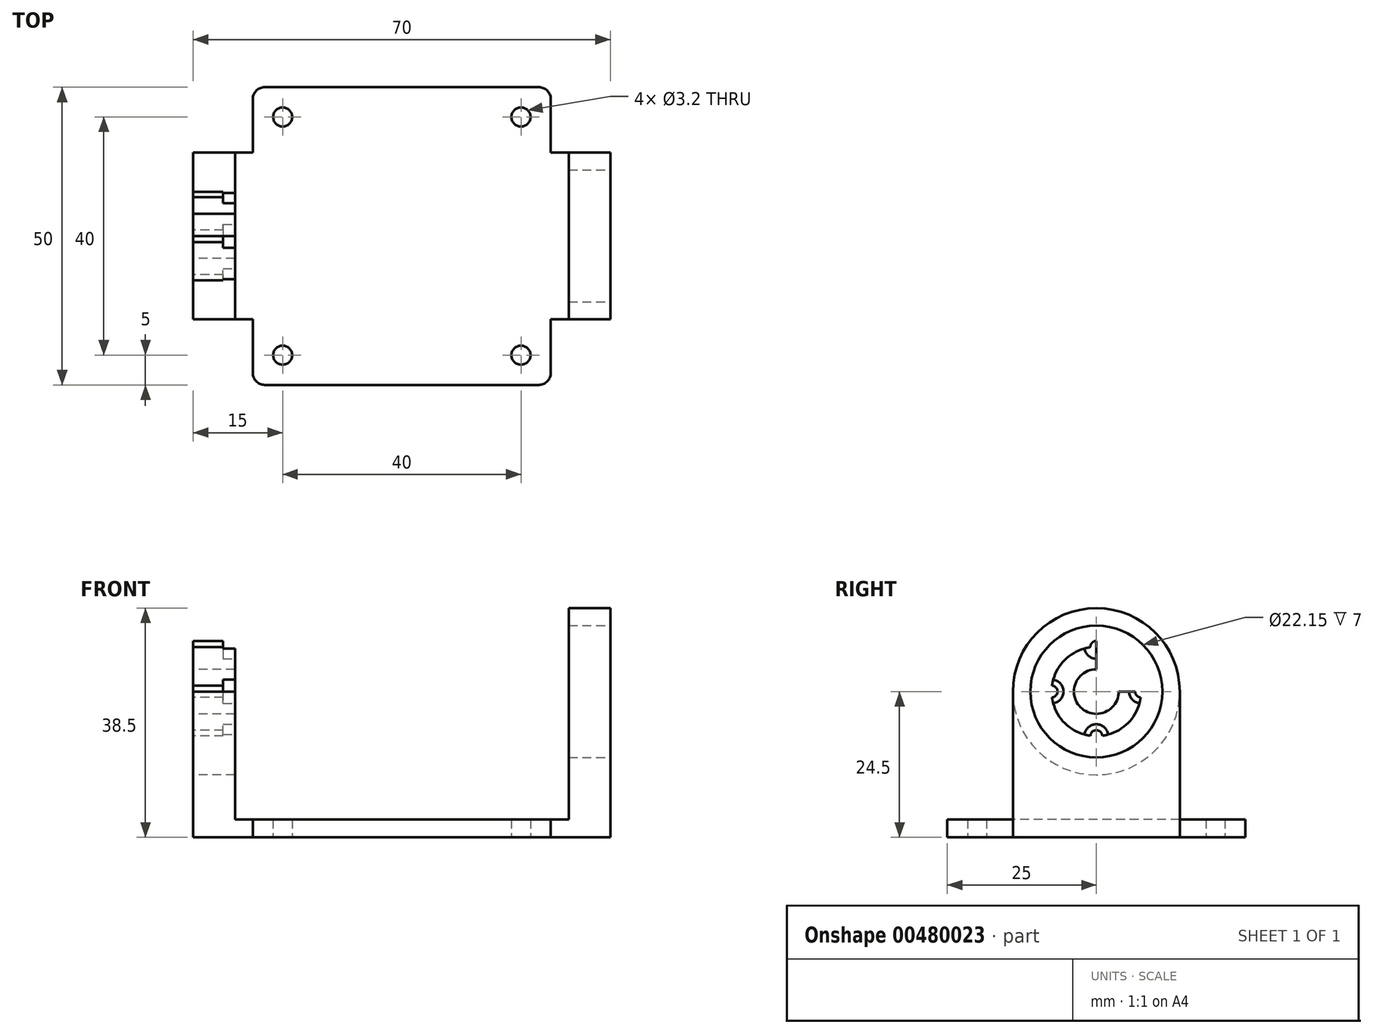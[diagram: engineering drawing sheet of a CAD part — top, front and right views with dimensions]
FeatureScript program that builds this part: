
annotation { "Feature Type Name" : "Feature", "Feature Type Description" : "" }
export const myFeature = defineFeature(function(context is Context, id is Id, definition is map)
    precondition{}
    {
        {
            var Q0;
            Q0=qCreatedBy(makeId("Top.planeOp"),FACE);
            var sketch = newSketch(context, id + "F0", { "sketchPlane" : qUnion([Q0])});
            skLineSegment(sketch, "E0.bottom", {"start": v(23, 25) * mm, "end": v(-23, 25) * mm});
            skLineSegment(sketch, "E0.top", {"start": v(23, -25) * mm, "end": v(-23, -25) * mm});
            skLineSegment(sketch, "E0.left", {"start": v(25, 23) * mm, "end": v(25, -23) * mm});
            skLineSegment(sketch, "E0.right", {"start": v(-25, 23) * mm, "end": v(-25, -23) * mm});
            skPoint(sketch, "E0.middle", {"position": v(0, 0) * mm});
            skLineSegment(sketch, "E1.bottom", {"start": v(-20, 20) * mm, "end": v(20, 20) * mm});
            skLineSegment(sketch, "E1.top", {"start": v(-20, -20) * mm, "end": v(20, -20) * mm});
            skLineSegment(sketch, "E1.left", {"start": v(-20, 20) * mm, "end": v(-20, -20) * mm});
            skLineSegment(sketch, "E1.right", {"start": v(20, 20) * mm, "end": v(20, -20) * mm});
            skCircle(sketch, "E2", {"center": v(-20, 20) * mm, "radius": 1.6 * mm});
            skCircle(sketch, "E3", {"center": v(20, 20) * mm, "radius": 1.6 * mm});
            skCircle(sketch, "E4", {"center": v(-20, -20) * mm, "radius": 1.6 * mm});
            skCircle(sketch, "E5", {"center": v(20, -20) * mm, "radius": 1.6 * mm});
            skLineSegment(sketch, "E6.bottom", {"start": v(-25, 0) * mm, "end": v(-35, 0) * mm});
            skLineSegment(sketch, "E6.top", {"start": v(-25, 14) * mm, "end": v(-35, 14) * mm});
            skLineSegment(sketch, "E6.left", {"start": v(-25, 0) * mm, "end": v(-25, 14) * mm});
            skLineSegment(sketch, "E6.right", {"start": v(-35, 0) * mm, "end": v(-35, 14) * mm});
            skLineSegment(sketch, "E7.top", {"start": v(-25, -14) * mm, "end": v(-35, -14) * mm});
            skLineSegment(sketch, "E7.left", {"start": v(-25, 0) * mm, "end": v(-25, -14) * mm});
            skLineSegment(sketch, "E7.right", {"start": v(-35, 0) * mm, "end": v(-35, -14) * mm});
            skLineSegment(sketch, "E8.bottom", {"start": v(25, 0) * mm, "end": v(35, 0) * mm});
            skLineSegment(sketch, "E8.top", {"start": v(25, 14) * mm, "end": v(35, 14) * mm});
            skLineSegment(sketch, "E8.left", {"start": v(25, 0) * mm, "end": v(25, 14) * mm});
            skLineSegment(sketch, "E8.right", {"start": v(35, 0) * mm, "end": v(35, 14) * mm});
            skLineSegment(sketch, "E9.top", {"start": v(25, -14) * mm, "end": v(35, -14) * mm});
            skLineSegment(sketch, "E9.left", {"start": v(25, 0) * mm, "end": v(25, -14) * mm});
            skLineSegment(sketch, "E9.right", {"start": v(35, 0) * mm, "end": v(35, -14) * mm});
            skPoint(sketch, "E10.visualSharp", {"position": v(-25, 25) * mm});
            skArc(sketch, "E10.filletArc", {"start": v(-23, 25) * mm, "mid": v(-24.41, 24.41) * mm, "end": v(-25, 23) * mm});
            skPoint(sketch, "E11.visualSharp", {"position": v(-25, -25) * mm});
            skArc(sketch, "E11.filletArc", {"start": v(-25, -23) * mm, "mid": v(-24.41, -24.41) * mm, "end": v(-23, -25) * mm});
            skPoint(sketch, "E12.visualSharp", {"position": v(25, 25) * mm});
            skArc(sketch, "E12.filletArc", {"start": v(25, 23) * mm, "mid": v(24.41, 24.41) * mm, "end": v(23, 25) * mm});
            skPoint(sketch, "E13.visualSharp", {"position": v(25, -25) * mm});
            skArc(sketch, "E13.filletArc", {"start": v(23, -25) * mm, "mid": v(24.41, -24.41) * mm, "end": v(25, -23) * mm});
            skSolve(sketch);
        }
        {
            var Q0;
            Q0 = qSketchRegion(id + "F0", true);
            var Q1;
            {var subQ5=sQuery(id+"F0.wireOp",EDGE,"E2");var subQ13=sQuery(id+"F0.wireOp",EDGE,"E1.bottom");var subQ14=makeQuery(id+"F0.imprint","INTERSECT",VERTEX,{"derivedFrom":[subQ13,subQ5]});Q1=makeQuery(id+"F0.imprint","IMPRINT",FACE,{"disambiguationData":[TD([[makeQuery(id+"F0.imprint","IMPRINT",EDGE,{"disambiguationData":[TD([[subQ14,-1.0]])],"derivedFrom":subQ13}),-1.0]])]});}
            extrude(context, id + "F1", {"entities" : qUnion([Q0, Q1]), "depth" : 3 * mm});
        }
        {
            var Q0;
            Q0=makeQuery(id+"F1.opExtrude","CAP_FACE",FACE,{"disambiguationData":[OSD([sQuery(id+"F0.wireOp",EDGE,"E0.bottom"),sQuery(id+"F0.wireOp",EDGE,"E0.top"),sQuery(id+"F0.wireOp",EDGE,"E0.left"),sQuery(id+"F0.wireOp",EDGE,"E0.right"),sQuery(id+"F0.wireOp",EDGE,"E2"),sQuery(id+"F0.wireOp",EDGE,"E3"),sQuery(id+"F0.wireOp",EDGE,"E4"),sQuery(id+"F0.wireOp",EDGE,"E5"),sQuery(id+"F0.wireOp",EDGE,"E6.top"),sQuery(id+"F0.wireOp",EDGE,"E6.right"),sQuery(id+"F0.wireOp",EDGE,"E7.top"),sQuery(id+"F0.wireOp",EDGE,"E7.right"),sQuery(id+"F0.wireOp",EDGE,"E8.top"),sQuery(id+"F0.wireOp",EDGE,"E8.right"),sQuery(id+"F0.wireOp",EDGE,"E9.top"),sQuery(id+"F0.wireOp",EDGE,"E9.right"),sQuery(id+"F0.wireOp",EDGE,"E10.filletArc"),sQuery(id+"F0.wireOp",EDGE,"E11.filletArc"),sQuery(id+"F0.wireOp",EDGE,"E12.filletArc"),sQuery(id+"F0.wireOp",EDGE,"E13.filletArc")])],"isStart":false});
            var sketch = newSketch(context, id + "F2", { "sketchPlane" : qUnion([Q0])});
            skLineSegment(sketch, "E14.bottom", {"start": v(-35, 14) * mm, "end": v(-28, 14) * mm});
            skLineSegment(sketch, "E14.top", {"start": v(-35, -14) * mm, "end": v(-28, -14) * mm});
            skLineSegment(sketch, "E14.left", {"start": v(-35, 14) * mm, "end": v(-35, -14) * mm});
            skLineSegment(sketch, "E14.right", {"start": v(-28, 14) * mm, "end": v(-28, -14) * mm});
            skLineSegment(sketch, "E15.bottom", {"start": v(35, 14) * mm, "end": v(28, 14) * mm});
            skLineSegment(sketch, "E15.top", {"start": v(35, -14) * mm, "end": v(28, -14) * mm});
            skLineSegment(sketch, "E15.left", {"start": v(35, 14) * mm, "end": v(35, -14) * mm});
            skLineSegment(sketch, "E15.right", {"start": v(28, 14) * mm, "end": v(28, -14) * mm});
            skSolve(sketch);
        }
        {
            var Q0;
            Q0 = qSketchRegion(id + "F2", true);
            extrude(context, id + "F3", {"entities" : qUnion([Q0]), "operationType" : NewBodyOperationType.ADD, "depth" : (32 + 3.5) * mm});
        }
        {
            var Q0;
            Q0=makeQuery(id+"F3.boolean.opBoolean","MERGE",FACE,{"derivedFrom":[makeQuery(id+"F1.opExtrude","SWEPT_FACE",FACE,{"disambiguationData":[OSD([sQuery(id+"F0.wireOp",EDGE,"E6.right"),sQuery(id+"F0.wireOp",EDGE,"E7.right")])]}),makeQuery(id+"F3.opExtrude","SWEPT_FACE",FACE,{"disambiguationData":[OSD([sQuery(id+"F2.wireOp",EDGE,"E14.left")])]})]});
            var sketch = newSketch(context, id + "F4", { "sketchPlane" : qUnion([Q0])});
            skLineSegment(sketch, "E16", {"start": v(0, 38.5) * mm, "end": v(0, 24.5) * mm});
            skPoint(sketch, "E16.endSnap0", {"position": v(0, 38.5) * mm});
            skCircle(sketch, "E17", {"center": v(0, 24.5) * mm, "radius": 11 * mm});
            skCircle(sketch, "E18", {"center": v(0, 24.5) * mm, "radius": 14 * mm});
            skLineSegment(sketch, "E19.bottom", {"start": v(-14, 38.5) * mm, "end": v(14, 38.5) * mm});
            skLineSegment(sketch, "E19.top", {"start": v(-14, 0) * mm, "end": v(14, 0) * mm});
            skLineSegment(sketch, "E19.left", {"start": v(-14, 38.5) * mm, "end": v(-14, 0) * mm});
            skLineSegment(sketch, "E19.right", {"start": v(14, 38.5) * mm, "end": v(14, 0) * mm});
            skSolve(sketch);
        }
        {
            var Q0;
            {var subQ0=sQuery(id+"F4.wireOp",EDGE,"E19.bottom");var subQ1=sQuery(id+"F4.wireOp",EDGE,"E18");var subQ2=makeQuery(id+"F4.imprint","INTERSECT",VERTEX,{"derivedFrom":[subQ1,subQ0]});Q0=makeQuery(id+"F4.imprint","IMPRINT",FACE,{"disambiguationData":[TD([[makeQuery(id+"F4.imprint","IMPRINT",EDGE,{"disambiguationData":[TD([[subQ2,1.0]])],"derivedFrom":subQ1}),-1.0]])]});}
            var Q1;
            {var subQ0=sQuery(id+"F4.wireOp",EDGE,"E19.bottom");var subQ1=sQuery(id+"F4.wireOp",EDGE,"E18");var subQ2=makeQuery(id+"F4.imprint","INTERSECT",VERTEX,{"derivedFrom":[subQ1,subQ0]});Q1=makeQuery(id+"F4.imprint","IMPRINT",FACE,{"disambiguationData":[TD([[makeQuery(id+"F4.imprint","IMPRINT",EDGE,{"disambiguationData":[TD([[subQ2,-1.0]])],"derivedFrom":subQ1}),-1.0]])]});}
            extrude(context, id + "F5", {"entities" : qUnion([Q0, Q1]), "operationType" : NewBodyOperationType.REMOVE, "endBound" : BoundingType.THROUGH_ALL, "oppositeDirection" : true, "depth" : 25 * mm});
        }
        {
            var Q0;
            Q0=makeQuery(id+"F3.boolean.opBoolean","MERGE",FACE,{"derivedFrom":[makeQuery(id+"F1.opExtrude","SWEPT_FACE",FACE,{"disambiguationData":[OSD([sQuery(id+"F0.wireOp",EDGE,"E8.right"),sQuery(id+"F0.wireOp",EDGE,"E9.right")])]}),makeQuery(id+"F3.opExtrude","SWEPT_FACE",FACE,{"disambiguationData":[OSD([sQuery(id+"F2.wireOp",EDGE,"E15.left")])]})]});
            var sketch = newSketch(context, id + "F6", { "sketchPlane" : qUnion([Q0])});
            skCircle(sketch, "E20", {"center": v(0, 24.5) * mm, "radius": 14 * mm});
            skPoint(sketch, "E20.first.point", {"position": v(-14, 24.5) * mm});
            skPoint(sketch, "E20.second.point", {"position": v(0, 38.5) * mm});
            skPoint(sketch, "E20.third.point", {"position": v(14, 24.5) * mm});
            skCircle(sketch, "E21", {"center": v(0, 24.5) * mm, "radius": 11.07 * mm});
            skSolve(sketch);
        }
        {
            var Q0;
            Q0=makeQuery(id+"F6.imprint","IMPRINT",FACE,{"disambiguationData":[TD([[makeQuery(id+"F6.imprint","IMPRINT",EDGE,{"derivedFrom":sQuery(id+"F6.wireOp",EDGE,"E21")}),1.0]])]});
            extrude(context, id + "F7", {"entities" : qUnion([Q0]), "operationType" : NewBodyOperationType.REMOVE, "endBound" : BoundingType.UP_TO_NEXT, "oppositeDirection" : true, "depth" : 25 * mm});
        }
        {
            var Q0;
            Q0=makeQuery(id+"F3.boolean.opBoolean","MERGE",FACE,{"derivedFrom":[makeQuery(id+"F1.opExtrude","SWEPT_FACE",FACE,{"disambiguationData":[OSD([sQuery(id+"F0.wireOp",EDGE,"E6.right"),sQuery(id+"F0.wireOp",EDGE,"E7.right")])]}),makeQuery(id+"F3.opExtrude","SWEPT_FACE",FACE,{"disambiguationData":[OSD([sQuery(id+"F2.wireOp",EDGE,"E14.left")])]})]});
            var sketch = newSketch(context, id + "F8", { "sketchPlane" : qUnion([Q0])});
            skCircle(sketch, "E22", {"center": v(0, 24.5) * mm, "radius": 14 * mm});
            skPoint(sketch, "E22.first.point", {"position": v(-14, 24.5) * mm});
            skPoint(sketch, "E22.second.point", {"position": v(0, 38.5) * mm});
            skPoint(sketch, "E22.third.point", {"position": v(14, 24.5) * mm});
            skCircle(sketch, "E23", {"center": v(0, 24.5) * mm, "radius": 7.5 * mm});
            skLineSegment(sketch, "E24", {"start": v(0, 38.5) * mm, "end": v(0, 17) * mm});
            skLineSegment(sketch, "E25", {"start": v(0, 24.5) * mm, "end": v(7.5, 24.5) * mm});
            skLineSegment(sketch, "E26", {"start": v(0, 24.5) * mm, "end": v(-7.5, 24.5) * mm});
            skCircle(sketch, "E27", {"center": v(0, 32) * mm, "radius": 1 * mm});
            skCircle(sketch, "E28", {"center": v(-7.5, 24.5) * mm, "radius": 1 * mm});
            skCircle(sketch, "E29", {"center": v(7.5, 24.5) * mm, "radius": 1 * mm});
            skCircle(sketch, "E30", {"center": v(0, 17) * mm, "radius": 1 * mm});
            skCircle(sketch, "E31", {"center": v(0, 24.5) * mm, "radius": 3.75 * mm});
            skSolve(sketch);
        }
        {
            var Q0;
            {var subQ1=sQuery(id+"F8.wireOp",EDGE,"E24");var subQ3=sQuery(id+"F8.wireOp",EDGE,"E31");var subQ4=makeQuery(id+"F8.imprint","INTERSECT",VERTEX,{"disambiguationData":[OD(1.0)],"derivedFrom":[subQ1,subQ3]});Q0=makeQuery(id+"F8.imprint","IMPRINT",FACE,{"disambiguationData":[TD([[makeQuery(id+"F8.imprint","IMPRINT",EDGE,{"disambiguationData":[TD([[subQ4,1.0]])],"derivedFrom":subQ3}),1.0]])]});}
            var Q1;
            {var subQ1=sQuery(id+"F8.wireOp",EDGE,"E24");var subQ3=sQuery(id+"F8.wireOp",EDGE,"E31");var subQ4=makeQuery(id+"F8.imprint","INTERSECT",VERTEX,{"disambiguationData":[OD(0.0)],"derivedFrom":[subQ1,subQ3]});Q1=makeQuery(id+"F8.imprint","IMPRINT",FACE,{"disambiguationData":[TD([[makeQuery(id+"F8.imprint","IMPRINT",EDGE,{"disambiguationData":[TD([[subQ4,-1.0]])],"derivedFrom":subQ3}),1.0]])]});}
            var Q2;
            {var subQ1=sQuery(id+"F8.wireOp",EDGE,"E24");var subQ3=sQuery(id+"F8.wireOp",EDGE,"E31");var subQ4=makeQuery(id+"F8.imprint","INTERSECT",VERTEX,{"disambiguationData":[OD(0.0)],"derivedFrom":[subQ1,subQ3]});Q2=makeQuery(id+"F8.imprint","IMPRINT",FACE,{"disambiguationData":[TD([[makeQuery(id+"F8.imprint","IMPRINT",EDGE,{"disambiguationData":[TD([[subQ4,1.0]])],"derivedFrom":subQ3}),1.0]])]});}
            var Q3;
            {var subQ1=sQuery(id+"F8.wireOp",EDGE,"E24");var subQ3=sQuery(id+"F8.wireOp",EDGE,"E31");var subQ4=makeQuery(id+"F8.imprint","INTERSECT",VERTEX,{"disambiguationData":[OD(1.0)],"derivedFrom":[subQ1,subQ3]});Q3=makeQuery(id+"F8.imprint","IMPRINT",FACE,{"disambiguationData":[TD([[makeQuery(id+"F8.imprint","IMPRINT",EDGE,{"disambiguationData":[TD([[subQ4,-1.0]])],"derivedFrom":subQ3}),1.0]])]});}
            var Q4;
            {var subQ0=sQuery(id+"F8.wireOp",EDGE,"E23");var subQ1=makeQuery(id+"F8.imprint","INTERSECT",VERTEX,{"derivedFrom":[subQ0,sQuery(id+"F8.wireOp",EDGE,"E26")]});Q4=makeQuery(id+"F8.imprint","IMPRINT",FACE,{"disambiguationData":[TD([[makeQuery(id+"F8.imprint","IMPRINT",EDGE,{"disambiguationData":[TD([[subQ1,1.0]])],"derivedFrom":subQ0}),-1.0]])]});}
            var Q5;
            {var subQ0=sQuery(id+"F8.wireOp",EDGE,"E26");var subQ1=sQuery(id+"F8.wireOp",EDGE,"E23");var subQ2=makeQuery(id+"F8.imprint","INTERSECT",VERTEX,{"derivedFrom":[subQ1,subQ0]});Q5=makeQuery(id+"F8.imprint","IMPRINT",FACE,{"disambiguationData":[TD([[makeQuery(id+"F8.imprint","IMPRINT",EDGE,{"disambiguationData":[TD([[subQ2,1.0]])],"derivedFrom":subQ1}),1.0]])]});}
            var Q6;
            {var subQ0=sQuery(id+"F8.wireOp",EDGE,"E26");var subQ1=sQuery(id+"F8.wireOp",EDGE,"E23");var subQ2=makeQuery(id+"F8.imprint","INTERSECT",VERTEX,{"derivedFrom":[subQ1,subQ0]});Q6=makeQuery(id+"F8.imprint","IMPRINT",FACE,{"disambiguationData":[TD([[makeQuery(id+"F8.imprint","IMPRINT",EDGE,{"disambiguationData":[TD([[subQ2,-1.0]])],"derivedFrom":subQ1}),1.0]])]});}
            var Q7;
            {var subQ0=sQuery(id+"F8.wireOp",EDGE,"E24");var subQ1=sQuery(id+"F8.wireOp",EDGE,"E23");var subQ2=makeQuery(id+"F8.imprint","INTERSECT",VERTEX,{"disambiguationData":[OD(1.0)],"derivedFrom":[subQ1,subQ0]});Q7=makeQuery(id+"F8.imprint","IMPRINT",FACE,{"disambiguationData":[TD([[makeQuery(id+"F8.imprint","IMPRINT",EDGE,{"disambiguationData":[TD([[subQ2,-1.0]])],"derivedFrom":subQ1}),-1.0]])]});}
            var Q8;
            {var subQ0=sQuery(id+"F8.wireOp",EDGE,"E24");var subQ1=sQuery(id+"F8.wireOp",EDGE,"E23");var subQ2=makeQuery(id+"F8.imprint","INTERSECT",VERTEX,{"disambiguationData":[OD(1.0)],"derivedFrom":[subQ1,subQ0]});Q8=makeQuery(id+"F8.imprint","IMPRINT",FACE,{"disambiguationData":[TD([[makeQuery(id+"F8.imprint","IMPRINT",EDGE,{"disambiguationData":[TD([[subQ2,-1.0]])],"derivedFrom":subQ1}),1.0]])]});}
            var Q9;
            {var subQ0=sQuery(id+"F8.wireOp",EDGE,"E27");var subQ1=sQuery(id+"F8.wireOp",EDGE,"E23");var subQ2=makeQuery(id+"F8.imprint","INTERSECT",VERTEX,{"disambiguationData":[OD(0.0)],"derivedFrom":[subQ1,subQ0]});Q9=makeQuery(id+"F8.imprint","IMPRINT",FACE,{"disambiguationData":[TD([[makeQuery(id+"F8.imprint","IMPRINT",EDGE,{"disambiguationData":[TD([[subQ2,-1.0]])],"derivedFrom":subQ1}),1.0]])]});}
            var Q10;
            {var subQ0=sQuery(id+"F8.wireOp",EDGE,"E27");var subQ1=sQuery(id+"F8.wireOp",EDGE,"E23");var subQ2=makeQuery(id+"F8.imprint","INTERSECT",VERTEX,{"disambiguationData":[OD(0.0)],"derivedFrom":[subQ1,subQ0]});Q10=makeQuery(id+"F8.imprint","IMPRINT",FACE,{"disambiguationData":[TD([[makeQuery(id+"F8.imprint","IMPRINT",EDGE,{"disambiguationData":[TD([[subQ2,-1.0]])],"derivedFrom":subQ1}),-1.0]])]});}
            var Q11;
            {var subQ0=sQuery(id+"F8.wireOp",EDGE,"E24");var subQ1=sQuery(id+"F8.wireOp",EDGE,"E23");var subQ2=makeQuery(id+"F8.imprint","INTERSECT",VERTEX,{"disambiguationData":[OD(0.0)],"derivedFrom":[subQ1,subQ0]});Q11=makeQuery(id+"F8.imprint","IMPRINT",FACE,{"disambiguationData":[TD([[makeQuery(id+"F8.imprint","IMPRINT",EDGE,{"disambiguationData":[TD([[subQ2,-1.0]])],"derivedFrom":subQ1}),1.0]])]});}
            var Q12;
            {var subQ0=sQuery(id+"F8.wireOp",EDGE,"E23");var subQ1=makeQuery(id+"F8.imprint","INTERSECT",VERTEX,{"disambiguationData":[OD(0.0)],"derivedFrom":[subQ0,sQuery(id+"F8.wireOp",EDGE,"E24")]});Q12=makeQuery(id+"F8.imprint","IMPRINT",FACE,{"disambiguationData":[TD([[makeQuery(id+"F8.imprint","IMPRINT",EDGE,{"disambiguationData":[TD([[subQ1,1.0]])],"derivedFrom":subQ0}),-1.0]])]});}
            var Q13;
            {var subQ0=sQuery(id+"F8.wireOp",EDGE,"E24");var subQ1=sQuery(id+"F8.wireOp",EDGE,"E23");var subQ2=makeQuery(id+"F8.imprint","INTERSECT",VERTEX,{"disambiguationData":[OD(0.0)],"derivedFrom":[subQ1,subQ0]});Q13=makeQuery(id+"F8.imprint","IMPRINT",FACE,{"disambiguationData":[TD([[makeQuery(id+"F8.imprint","IMPRINT",EDGE,{"disambiguationData":[TD([[subQ2,1.0]])],"derivedFrom":subQ1}),1.0]])]});}
            var Q14;
            {var subQ0=sQuery(id+"F8.wireOp",EDGE,"E23");var subQ1=makeQuery(id+"F8.imprint","INTERSECT",VERTEX,{"derivedFrom":[subQ0,sQuery(id+"F8.wireOp",EDGE,"E25")]});Q14=makeQuery(id+"F8.imprint","IMPRINT",FACE,{"disambiguationData":[TD([[makeQuery(id+"F8.imprint","IMPRINT",EDGE,{"disambiguationData":[TD([[subQ1,-1.0]])],"derivedFrom":subQ0}),-1.0]])]});}
            var Q15;
            {var subQ0=sQuery(id+"F8.wireOp",EDGE,"E25");var subQ1=sQuery(id+"F8.wireOp",EDGE,"E23");var subQ2=makeQuery(id+"F8.imprint","INTERSECT",VERTEX,{"derivedFrom":[subQ1,subQ0]});Q15=makeQuery(id+"F8.imprint","IMPRINT",FACE,{"disambiguationData":[TD([[makeQuery(id+"F8.imprint","IMPRINT",EDGE,{"disambiguationData":[TD([[subQ2,-1.0]])],"derivedFrom":subQ1}),1.0]])]});}
            var Q16;
            {var subQ0=sQuery(id+"F8.wireOp",EDGE,"E25");var subQ1=sQuery(id+"F8.wireOp",EDGE,"E23");var subQ2=makeQuery(id+"F8.imprint","INTERSECT",VERTEX,{"derivedFrom":[subQ1,subQ0]});Q16=makeQuery(id+"F8.imprint","IMPRINT",FACE,{"disambiguationData":[TD([[makeQuery(id+"F8.imprint","IMPRINT",EDGE,{"disambiguationData":[TD([[subQ2,1.0]])],"derivedFrom":subQ1}),1.0]])]});}
            extrude(context, id + "F9", {"entities" : qUnion([Q0, Q1, Q2, Q3, Q4, Q5, Q6, Q7, Q8, Q9, Q10, Q11, Q12, Q13, Q14, Q15, Q16]), "operationType" : NewBodyOperationType.REMOVE, "oppositeDirection" : true, "depth" : 25 * mm});
        }
        {
            var Q0;
            Q0=makeQuery(id+"F3.opExtrude","SWEPT_FACE",FACE,{"disambiguationData":[OSD([sQuery(id+"F2.wireOp",EDGE,"E14.right")])]});
            var sketch = newSketch(context, id + "F10", { "sketchPlane" : qUnion([Q0])});
            skCircle(sketch, "E32", {"center": v(-7.5, 24.5) * mm, "radius": 2 * mm});
            skCircle(sketch, "E33", {"center": v(0, 17) * mm, "radius": 2 * mm});
            skCircle(sketch, "E34", {"center": v(0, 32) * mm, "radius": 2 * mm});
            skCircle(sketch, "E35", {"center": v(7.5, 24.5) * mm, "radius": 2 * mm});
            skSolve(sketch);
        }
        {
            var Q0;
            Q0 = qSketchRegion(id + "F10", true);
            extrude(context, id + "F11", {"entities" : qUnion([Q0]), "operationType" : NewBodyOperationType.REMOVE, "oppositeDirection" : true, "depth" : 2 * mm});
        }
    });
